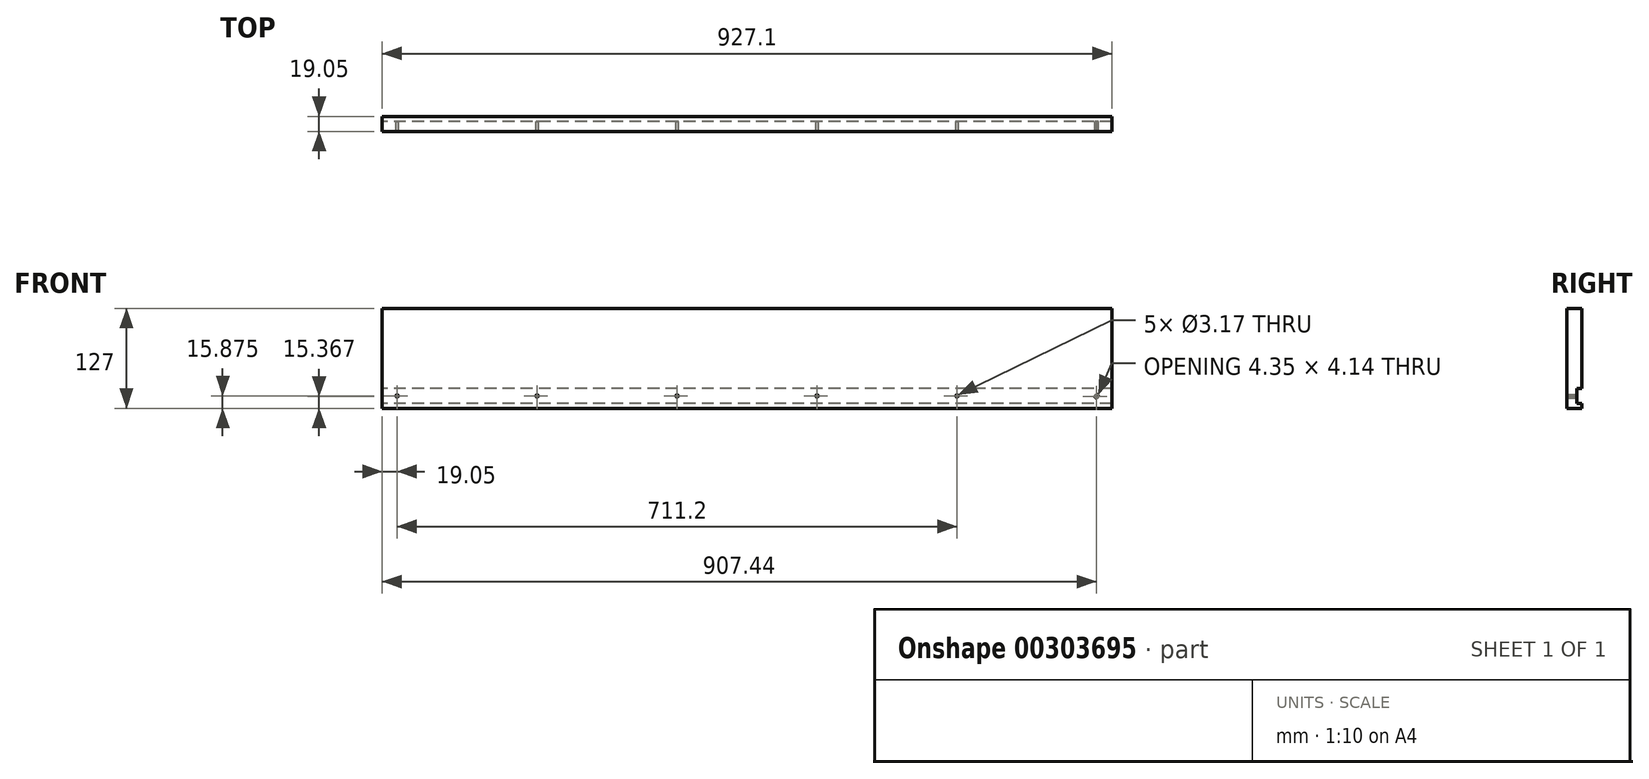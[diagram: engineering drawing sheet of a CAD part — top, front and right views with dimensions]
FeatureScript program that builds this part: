
annotation { "Feature Type Name" : "Feature", "Feature Type Description" : "" }
export const myFeature = defineFeature(function(context is Context, id is Id, definition is map)
    precondition{}
    {
        {
            var Q0;
            Q0=qCreatedBy(makeId("Front.planeOp"),FACE);
            var sketch = newSketch(context, id + "F0", { "sketchPlane" : qUnion([Q0])});
            skLineSegment(sketch, "E0.bottom", {"start": v(0, 0) * mm, "end": v(927.1, 0) * mm});
            skLineSegment(sketch, "E0.top", {"start": v(0, -127) * mm, "end": v(927.1, -127) * mm});
            skLineSegment(sketch, "E0.left", {"start": v(0, 0) * mm, "end": v(0, -127) * mm});
            skLineSegment(sketch, "E0.right", {"start": v(927.1, 0) * mm, "end": v(927.1, -127) * mm});
            skSolve(sketch);
        }
        {
            var Q0;
            Q0=qSketchRegion(id+"F0",true);
            extrude(context, id + "F1", {"entities" : qUnion([Q0]), "depth" : 19.05 * mm});
        }
        {
            var Q0;
            Q0=qCreatedBy(makeId("Front.planeOp"),FACE);
            var sketch = newSketch(context, id + "F2", { "sketchPlane" : qUnion([Q0])});
            skLineSegment(sketch, "E1.bottom", {"start": v(927.1, -101.6) * mm, "end": v(0, -101.6) * mm});
            skLineSegment(sketch, "E1.top", {"start": v(927.1, -120.65) * mm, "end": v(0, -120.65) * mm});
            skLineSegment(sketch, "E1.left", {"start": v(927.1, -101.6) * mm, "end": v(927.1, -120.65) * mm});
            skLineSegment(sketch, "E1.right", {"start": v(0, -101.6) * mm, "end": v(0, -120.65) * mm});
            skSolve(sketch);
        }
        {
            var Q0;
            Q0 = qSketchRegion(id + "F2", true);
            extrude(context, id + "F3", {"entities" : qUnion([Q0]), "operationType" : NewBodyOperationType.REMOVE, "depth" : 6.35 * mm});
        }
        {
            var Q0;
            Q0=qCreatedBy(makeId("Front.planeOp"),FACE);
            var sketch = newSketch(context, id + "F4", { "sketchPlane" : qUnion([Q0])});
            skCircle(sketch, "E2", {"center": v(908.05, -111.12) * mm, "radius": 1.59 * mm});
            skCircle(sketch, "E3", {"center": v(906.83, -112.14) * mm, "radius": 1.59 * mm});
            skCircle(sketch, "E4.1.0.0", {"center": v(730.25, -111.12) * mm, "radius": 1.59 * mm});
            skCircle(sketch, "E4.2.0.0", {"center": v(552.45, -111.12) * mm, "radius": 1.59 * mm});
            skCircle(sketch, "E4.3.0.0", {"center": v(374.65, -111.12) * mm, "radius": 1.59 * mm});
            skCircle(sketch, "E4.4.0.0", {"center": v(196.85, -111.12) * mm, "radius": 1.59 * mm});
            skCircle(sketch, "E4.5.0.0", {"center": v(19.05, -111.12) * mm, "radius": 1.59 * mm});
            skLineSegment(sketch, "E4.direction1", {"start": v(895.35, -111.12) * mm, "end": v(717.55, -111.12) * mm, "construction": true});
            skSolve(sketch);
        }
        {
            var Q0;
            Q0 = qSketchRegion(id + "F4", true);
            extrude(context, id + "F5", {"entities" : qUnion([Q0]), "operationType" : NewBodyOperationType.REMOVE, "endBound" : BoundingType.THROUGH_ALL, "depth" : 25.4 * mm, "offsetDistance" : 25.4 * mm});
        }
    });
